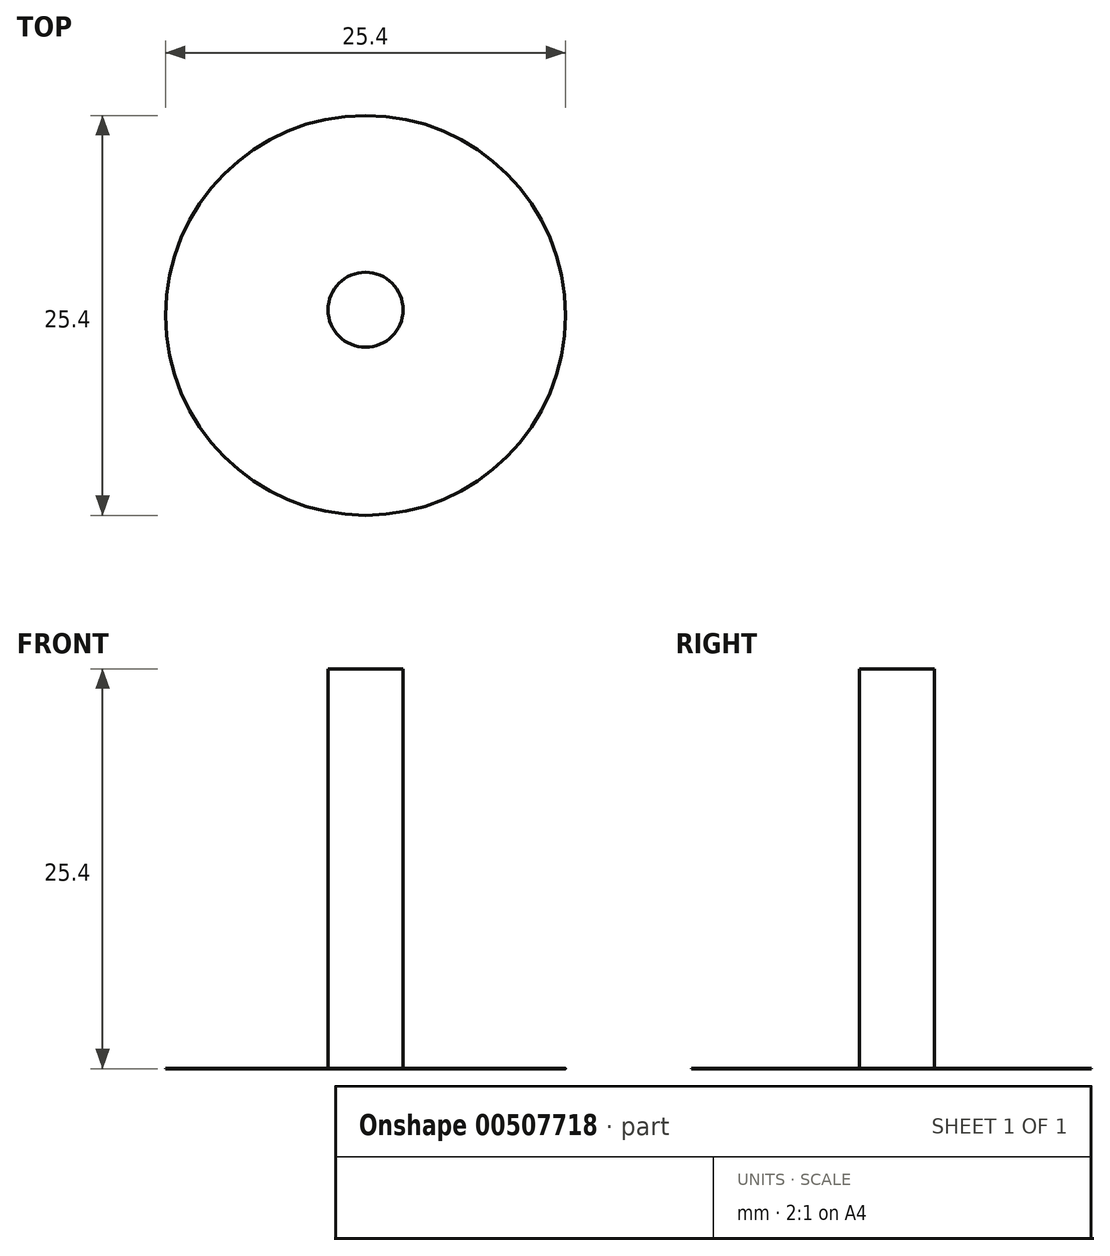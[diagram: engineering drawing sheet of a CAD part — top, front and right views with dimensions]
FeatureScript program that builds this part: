
annotation { "Feature Type Name" : "Feature", "Feature Type Description" : "" }
export const myFeature = defineFeature(function(context is Context, id is Id, definition is map)
    precondition{}
    {
        {
            var Q0;
            Q0=qCreatedBy(makeId("Top.planeOp"),FACE);
            var sketch = newSketch(context, id + "F0", { "sketchPlane" : qUnion([Q0])});
            skCircle(sketch, "E0", {"center": v(0, 0) * mm, "radius": 12.7 * mm});
            skSolve(sketch);
        }
        {
            var Q0;
            Q0=makeQuery(id+"F0.imprint","IMPRINT",FACE,{"disambiguationData":[TD([[makeQuery(id+"F0.imprint","IMPRINT",EDGE,{"derivedFrom":sQuery(id+"F0.wireOp",EDGE,"E0")}),1.0]])]});
            var Q1;
            Q1=sQuery(id+"F0.wireOp",EDGE,"E0");
            extrude(context, id + "F1", {"entities" : qUnion([Q0]), "surfaceEntities" : qUnion([Q1]), "offsetDistance" : 25.4 * mm, "depth" : 1 / 101.6 * mm});
        }
        {
            var Q0;
            Q0=qCreatedBy(makeId("Top.planeOp"),FACE);
            var sketch = newSketch(context, id + "F2", { "sketchPlane" : qUnion([Q0])});
            skCircle(sketch, "E1", {"center": v(0, 0.35) * mm, "radius": 2.38 * mm});
            skSolve(sketch);
        }
        {
            var Q0;
            Q0=makeQuery(id+"F2.imprint","IMPRINT",FACE,{"disambiguationData":[TD([[makeQuery(id+"F2.imprint","IMPRINT",EDGE,{"derivedFrom":sQuery(id+"F2.wireOp",EDGE,"E1")}),1.0]])]});
            extrude(context, id + "F3", {"entities" : qUnion([Q0]), "operationType" : NewBodyOperationType.ADD, "offsetDistance" : 25.4 * mm, "depth" : 25.4 * mm});
        }
    });
